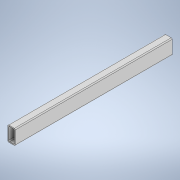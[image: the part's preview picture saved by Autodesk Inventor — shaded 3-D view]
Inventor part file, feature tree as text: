
AUTODESK INVENTOR PART (.ipt)
format: ipt  version: 2020 (Build 240168000, 168)  size: 122,368 bytes
history: native  units: in
note: dims shown in document units (in); Inventor stores cm internally (conversion verified against a paired STEP export)
features: extrude x1, sketch x1
ambient origin geometry x8: Origin, YZ Plane, XZ Plane, XY Plane, X Axis, Y Axis, Z Axis, Center Point
bodies: Solid1 (feature_tree)
feature tree (2):
  extrude  "Extrusion1"  Depth=1.0in
  sketch  "Sketch1"  dims[d0=2.0in d1=1.0in d2=0.125in d3=0.125in d4=0.125in d5=0.125in d6=0.125in d7=0.125in d8=0.125in d9=0.125in d10=0.125in d11=21.0in d12=0.0in]
